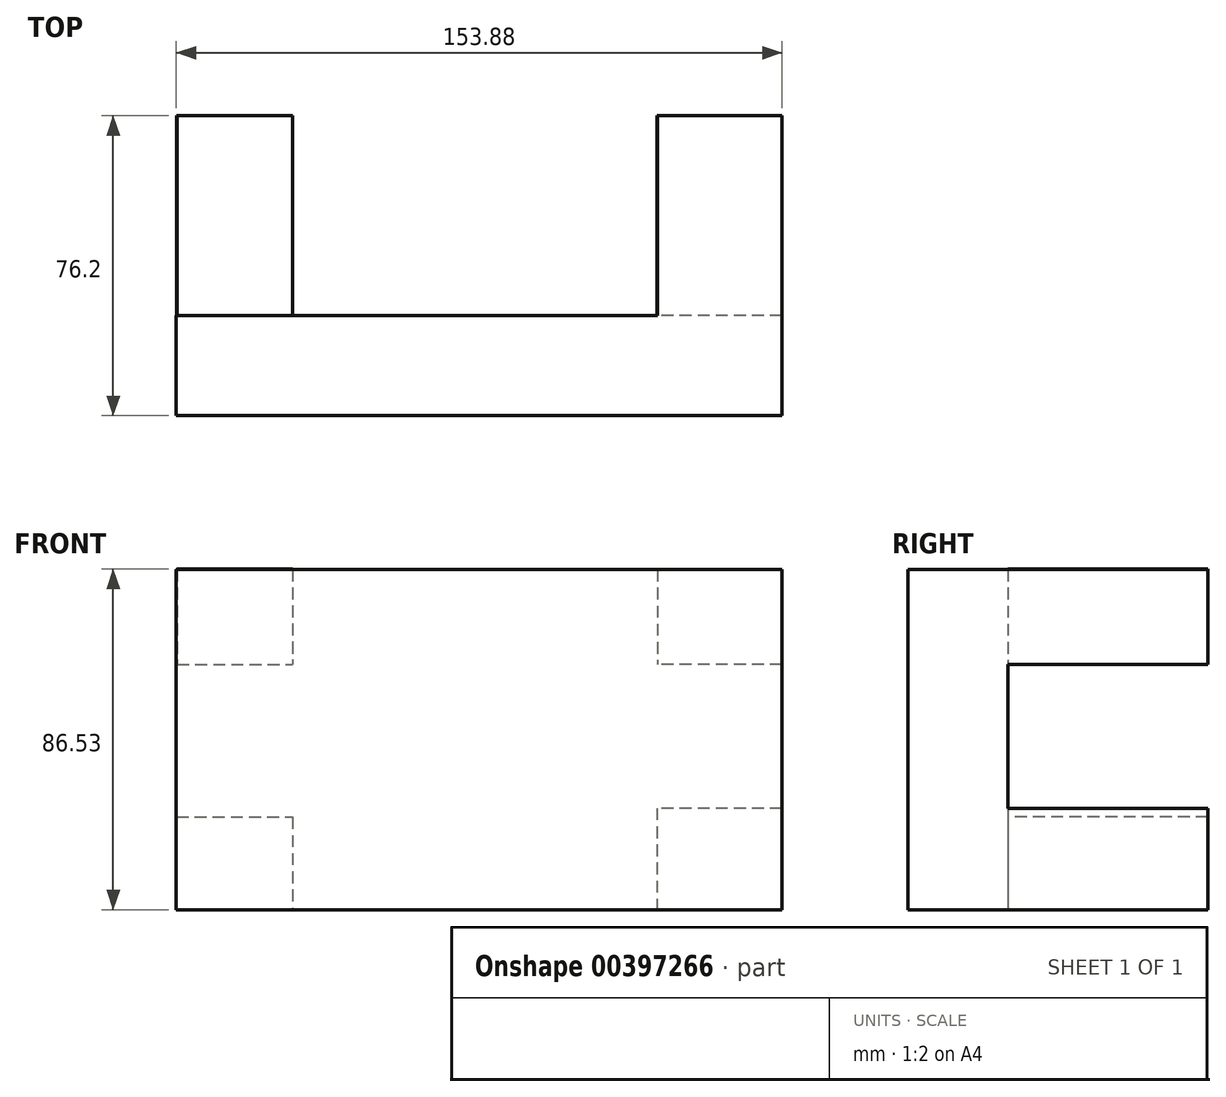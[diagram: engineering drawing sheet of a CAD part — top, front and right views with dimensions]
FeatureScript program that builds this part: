
annotation { "Feature Type Name" : "Feature", "Feature Type Description" : "" }
export const myFeature = defineFeature(function(context is Context, id is Id, definition is map)
    precondition{}
    {
        {
            var Q0;
            Q0=qCreatedBy(makeId("Front.planeOp"),FACE);
            var sketch = newSketch(context, id + "F0", { "sketchPlane" : qUnion([Q0])});
            skLineSegment(sketch, "E0.bottom", {"start": v(0, 0) * mm, "end": v(-153.88, 0) * mm});
            skLineSegment(sketch, "E0.top", {"start": v(0, 86.44) * mm, "end": v(-153.88, 86.44) * mm});
            skLineSegment(sketch, "E0.left", {"start": v(0, 0) * mm, "end": v(0, 86.44) * mm});
            skLineSegment(sketch, "E0.right", {"start": v(-153.88, 0) * mm, "end": v(-153.88, 86.44) * mm});
            skSolve(sketch);
        }
        {
            var Q0;
            Q0=makeQuery(id+"F0.imprint","IMPRINT",FACE,{"disambiguationData":[TD([[makeQuery(id+"F0.imprint","IMPRINT",EDGE,{"derivedFrom":sQuery(id+"F0.wireOp",EDGE,"E0.bottom")}),-1.0]])]});
            extrude(context, id + "F1", {"entities" : qUnion([Q0]), "depth" : 25.4 * mm});
        }
        {
            var Q0;
            Q0=qCreatedBy(makeId("Front.planeOp"),FACE);
            var sketch = newSketch(context, id + "F2", { "sketchPlane" : qUnion([Q0])});
            skLineSegment(sketch, "E1.bottom", {"start": v(0, 25.79) * mm, "end": v(-31.81, 25.79) * mm});
            skLineSegment(sketch, "E1.top", {"start": v(0, 0) * mm, "end": v(-31.81, 0) * mm});
            skLineSegment(sketch, "E1.left", {"start": v(0, 25.79) * mm, "end": v(0, 0) * mm});
            skLineSegment(sketch, "E1.right", {"start": v(-31.81, 25.79) * mm, "end": v(-31.81, 0) * mm});
            skLineSegment(sketch, "E2.bottom", {"start": v(0, 86.45) * mm, "end": v(-31.68, 86.45) * mm});
            skLineSegment(sketch, "E2.top", {"start": v(0, 62.34) * mm, "end": v(-31.68, 62.34) * mm});
            skLineSegment(sketch, "E2.left", {"start": v(0, 86.45) * mm, "end": v(0, 62.34) * mm});
            skLineSegment(sketch, "E2.right", {"start": v(-31.68, 86.45) * mm, "end": v(-31.68, 62.34) * mm});
            skLineSegment(sketch, "E3.bottom", {"start": v(-153.66, 86.53) * mm, "end": v(-124.35, 86.53) * mm});
            skLineSegment(sketch, "E3.top", {"start": v(-153.66, 62.34) * mm, "end": v(-124.35, 62.34) * mm});
            skLineSegment(sketch, "E3.left", {"start": v(-153.66, 86.53) * mm, "end": v(-153.66, 62.34) * mm});
            skLineSegment(sketch, "E3.right", {"start": v(-124.35, 86.53) * mm, "end": v(-124.35, 62.34) * mm});
            skLineSegment(sketch, "E4.bottom", {"start": v(-153.8, 23.54) * mm, "end": v(-124.35, 23.54) * mm});
            skLineSegment(sketch, "E4.top", {"start": v(-153.8, 0) * mm, "end": v(-124.35, 0) * mm});
            skLineSegment(sketch, "E4.left", {"start": v(-153.8, 23.54) * mm, "end": v(-153.8, 0) * mm});
            skLineSegment(sketch, "E4.right", {"start": v(-124.35, 23.54) * mm, "end": v(-124.35, 0) * mm});
            skSolve(sketch);
        }
        {
            var Q0;
            Q0=makeQuery(id+"F2.imprint","IMPRINT",FACE,{"disambiguationData":[TD([[makeQuery(id+"F2.imprint","IMPRINT",EDGE,{"derivedFrom":sQuery(id+"F2.wireOp",EDGE,"E1.bottom")}),1.0]])]});
            var Q1;
            Q1=makeQuery(id+"F2.imprint","IMPRINT",FACE,{"disambiguationData":[TD([[makeQuery(id+"F2.imprint","IMPRINT",EDGE,{"derivedFrom":sQuery(id+"F2.wireOp",EDGE,"E4.bottom")}),-1.0]])]});
            var Q2;
            Q2=makeQuery(id+"F2.imprint","IMPRINT",FACE,{"disambiguationData":[TD([[makeQuery(id+"F2.imprint","IMPRINT",EDGE,{"derivedFrom":sQuery(id+"F2.wireOp",EDGE,"E3.bottom")}),-1.0]])]});
            var Q3;
            Q3=makeQuery(id+"F2.imprint","IMPRINT",FACE,{"disambiguationData":[TD([[makeQuery(id+"F2.imprint","IMPRINT",EDGE,{"derivedFrom":sQuery(id+"F2.wireOp",EDGE,"E2.bottom")}),1.0]])]});
            extrude(context, id + "F3", {"entities" : qUnion([Q0, Q1, Q2, Q3]), "operationType" : NewBodyOperationType.ADD, "oppositeDirection" : true, "depth" : 50.8 * mm});
        }
        {
            var Q0;
            Q0=qCreatedBy(makeId("Front.planeOp"),FACE);
            var sketch = newSketch(context, id + "F4", { "sketchPlane" : qUnion([Q0])});
            skLineSegment(sketch, "E5.bottom", {"start": v(-125.6, 6.33) * mm, "end": v(-155.9, 6.33) * mm});
            skLineSegment(sketch, "E5.top", {"start": v(-125.6, 26.67) * mm, "end": v(-155.9, 26.67) * mm});
            skLineSegment(sketch, "E5.left", {"start": v(-125.6, 6.33) * mm, "end": v(-125.6, 26.67) * mm});
            skLineSegment(sketch, "E5.right", {"start": v(-155.9, 6.33) * mm, "end": v(-155.9, 26.67) * mm});
            skSolve(sketch);
        }
        {
            var Q1;
            Q1=makeQuery(id+"F3.opExtrude","SWEPT_FACE",FACE,{"disambiguationData":[OSD([sQuery(id+"F2.wireOp",EDGE,"E4.left")])]});
            var Q2;
            Q2=sQuery(id+"F4.wireOp",VERTEX,"E5.bottom.start");
            loft(context, id + "F5", {"operationType" : NewBodyOperationType.ADD, "sheetProfilesArray" : [{ "sheetProfileEntities" : qUnion([Q1]) }, { "sheetProfileEntities" : qUnion([Q2]) }]});
        }
    });
